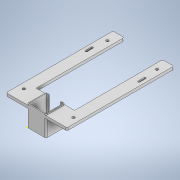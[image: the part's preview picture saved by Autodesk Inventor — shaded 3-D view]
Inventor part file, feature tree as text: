
AUTODESK INVENTOR PART (.ipt)
format: ipt  version: 2020 (Build 240168000, 168)  size: 293,888 bytes
history: native  units: in
note: dims shown in document units (in); Inventor stores cm internally (conversion verified against a paired STEP export)
features: sketch x8, extrude x7, fillet x3, plane x2, mirror x2, hole x1
ambient origin geometry x8: Origin, YZ Plane, XZ Plane, XY Plane, X Axis, Y Axis, Z Axis, Center Point
bodies: Solid1 (feature_tree)
feature tree (23):
  extrude  "Extrusion1"  Depth=1.8504in
  extrude  "Extrusion2"  Depth=1.9685in TaperAngle=0.0deg
  extrude  "Extrusion5"  Depth=2.0669in TaperAngle=0.0deg
  extrude  "Extrusion6"  Depth=8.6614in TaperAngle=0.0deg
  hole  "Hole1"  [1 undecoded]
  extrude  "Extrusion7"  Depth=0.3346in
  extrude  "Extrusion8"  Depth=0.1575in TaperAngle=0.0deg
  extrude  "Extrusion9"  Depth=0.3937in
  plane  "Work Plane2"
  mirror  "Mirror4"
  fillet  "Fillet5"  Radius=0.1772in
  fillet  "Fillet6"  Radius=0.5906in
  fillet  "Fillet7"  Radius=0.1575in
  plane  "Work Plane3"
  mirror  "Mirror5"
  sketch  "Sketch16"  dims[d50=0.1772in d51=0.3937in d53=0.1772in d54=0.5906in d55=0.1575in d56=0.0in d62=1.6929in d63=1.6929in d64=1.8504in d65=0.2559in d66=0.2559in d67=1.1811in d68=0.0787in d69=0.0in d71=0.1181in d72=0.1181in d73=0.1181in d74=0.1181in d76=2.4409in d77=2.4409in d78=1.1811in d75=0.0197in d79=0.0344in d80=0.0344in]
  sketch  "Sketch1"  dims[d0=1.8504in d1=1.8504in]
  sketch  "Sketch6"  dims[d2=2.0472in d3=0.0in d7=1.9685in d8=0.0in]
  sketch  "Sketch7"  dims[d26=0.2756in d27=2.0669in d28=0.0in]
  sketch  "Sketch8"  dims[d29=1.1024in d30=8.6614in d31=0.0in]
  sketch  "Sketch9"  dims[d36=0.1575in d37=0.2362in d38=0.2559in d39=0.1575in d40=90.0deg d41=0.315in d42=0.8108in d43=0.3346in]
  sketch  "Sketch10"  dims[d44=0.3937in d46=0.3346in]
  sketch  "Sketch11"  dims[d47=0.5906in d48=0.1575in d49=0.0in]
note: 1 required parameter value undecoded (feature->parameter linkage not recoverable at this tier; creation-order binding heuristic only, values carry confidence <= 0.55)
